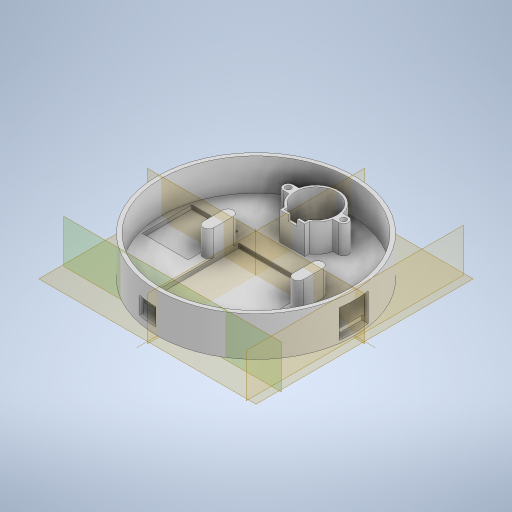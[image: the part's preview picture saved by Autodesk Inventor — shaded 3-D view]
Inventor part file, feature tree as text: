
AUTODESK INVENTOR PART (.ipt)
format: ipt  version: 2023 (Build 270158000, 158)  size: 430,592 bytes
history: native  units: in
note: dims shown in document units (in); Inventor stores cm internally (conversion verified against a paired STEP export)
features: extrude x10, sketch x10, plane x2
ambient origin geometry x8: Origin, YZ Plane, XZ Plane, XY Plane, X Axis, Y Axis, Z Axis, Center Point
bodies: Solid1 (feature_tree)
feature tree (22):
  extrude  "Extrusion1"  Depth=1.0827in TaperAngle=0.0deg
  extrude  "Extrusion2"  Depth=0.8858in TaperAngle=0.0deg
  extrude  "Extrusion3"  Depth=1.122in
  extrude  "Extrusion4"  Depth=0.689in
  extrude  "Extrusion5"  Depth=0.5709in
  extrude  "Extrusion6"  Depth=0.1181in
  extrude  "Extrusion7"  Depth=0.1575in TaperAngle=0.0deg
  extrude  "Extrusion8"  Depth=0.1575in
  plane  "Work Plane1"
  extrude  "Extrusion9"  Depth=0.748in
  plane  "Work Plane2"
  extrude  "Extrusion10"  Depth=1.2598in
  sketch  "Sketch1"  dims[d0=5.4134in d2=1.0827in d3=0.0in]
  sketch  "Sketch2"  dims[d4=5.1969in d5=0.8858in d6=0.0in]
  sketch  "Sketch3"  dims[d7=1.063in d8=1.122in]
  sketch  "Sketch4"  dims[d9=1.2402in d12=0.689in]
  sketch  "Sketch5"  dims[d14=0.0984in d15=0.5709in]
  sketch  "Sketch6"  dims[d16=0.7677in d17=0.0in d18=0.1181in]
  sketch  "Sketch7"  dims[d19=0.2362in d20=0.1575in d21=0.0in]
  sketch  "Sketch8"  dims[d24=0.1575in d25=0.1575in]
  sketch  "Sketch9"  dims[d26=0.748in d27=0.0in d28=1.1811in]
  sketch  "Sketch10"  dims[d29=0.6791in d30=1.2598in d31=90.0deg d32=1.3583in d33=0.1083in d34=0.0in d36=0.1476in d37=0.4134in d38=0.8268in d39=2.4606in d40=0.4134in d41=0.8268in d42=90.0deg d43=0.2953in d44=0.7087in d45=0.0in d46=0.4134in d47=2.126in d48=2.7008in d49=0.1181in d50=0.0in d52=0.4724in d53=0.4921in d54=4.0157in d55=0.0in d64=0.3937in d65=0.7874in d66=0.7874in d67=0.7874in d68=0.1969in d69=0.0in]
